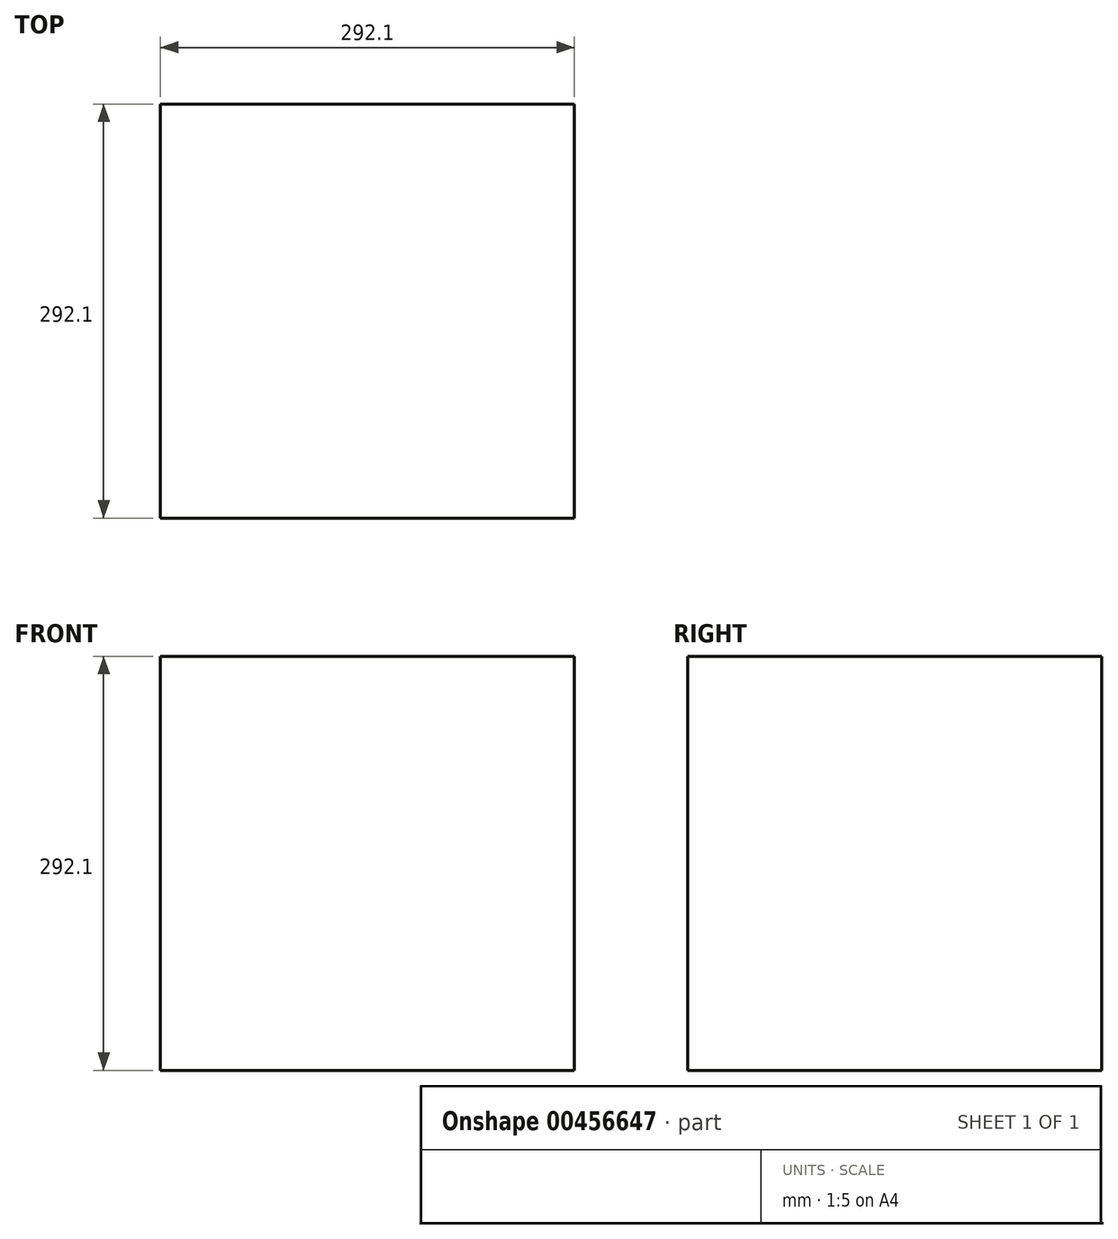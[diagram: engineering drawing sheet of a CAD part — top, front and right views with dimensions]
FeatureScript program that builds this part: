
annotation { "Feature Type Name" : "Feature", "Feature Type Description" : "" }
export const myFeature = defineFeature(function(context is Context, id is Id, definition is map)
    precondition{}
    {
        {
            var Q0;
            Q0=qCreatedBy(makeId("Front.planeOp"),FACE);
            var sketch = newSketch(context, id + "F0", { "sketchPlane" : qUnion([Q0])});
            skLineSegment(sketch, "E0.bottom", {"start": v(-157.07, 164.23) * mm, "end": v(135.03, 164.23) * mm});
            skLineSegment(sketch, "E0.top", {"start": v(-157.07, -127.87) * mm, "end": v(135.03, -127.87) * mm});
            skLineSegment(sketch, "E0.left", {"start": v(-157.07, 164.23) * mm, "end": v(-157.07, -127.87) * mm});
            skLineSegment(sketch, "E0.right", {"start": v(135.03, 164.23) * mm, "end": v(135.03, -127.87) * mm});
            skSolve(sketch);
        }
        {
            var Q0;
            Q0 = qSketchRegion(id + "F0", true);
            extrude(context, id + "F1", {"entities" : qUnion([Q0]), "depth" : 292.1 * mm});
        }
    });
